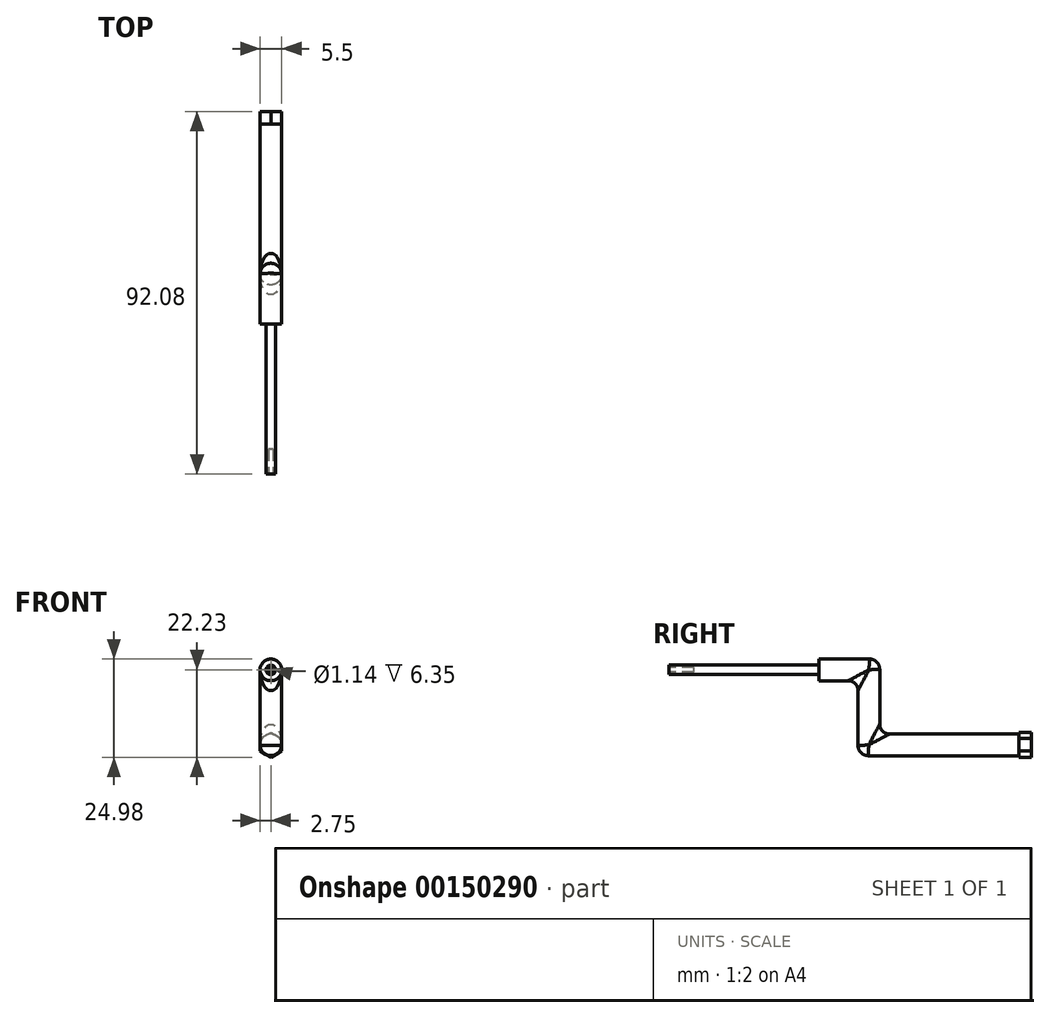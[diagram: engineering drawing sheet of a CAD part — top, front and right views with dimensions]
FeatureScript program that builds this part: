
annotation { "Feature Type Name" : "Feature", "Feature Type Description" : "" }
export const myFeature = defineFeature(function(context is Context, id is Id, definition is map)
    precondition{}
    {
        {
            var Q0;
            Q0=qCreatedBy(makeId("Front.planeOp"),FACE);
            var sketch = newSketch(context, id + "F0", { "sketchPlane" : qUnion([Q0])});
            skCircle(sketch, "E0.cCircle", {"center": v(0, 0) * mm, "radius": 3.18 * mm, "construction": true});
            skLineSegment(sketch, "E0.0", {"start": v(0, 3.18) * mm, "end": v(2.75, 1.59) * mm});
            skLineSegment(sketch, "E0.1", {"start": v(2.75, 1.59) * mm, "end": v(2.75, -1.59) * mm});
            skLineSegment(sketch, "E0.2", {"start": v(2.75, -1.59) * mm, "end": v(0, -3.18) * mm});
            skLineSegment(sketch, "E0.3", {"start": v(0, -3.18) * mm, "end": v(-2.75, -1.59) * mm});
            skLineSegment(sketch, "E0.4", {"start": v(-2.75, -1.59) * mm, "end": v(-2.75, 1.59) * mm});
            skLineSegment(sketch, "E0.5", {"start": v(-2.75, 1.59) * mm, "end": v(0, 3.18) * mm});
            skSolve(sketch);
        }
        {
            var Q0;
            Q0=makeQuery(id+"F0.imprint","IMPRINT",FACE,{"disambiguationData":[TD([[makeQuery(id+"F0.imprint","IMPRINT",EDGE,{"derivedFrom":sQuery(id+"F0.wireOp",EDGE,"E0.0")}),-1.0]])]});
            extrude(context, id + "F1", {"entities" : qUnion([Q0]), "depth" : 3.17 * mm});
        }
        {
            var Q0;
            Q0=makeQuery(id+"F1.opExtrude","CAP_FACE",FACE,{"disambiguationData":[OSD([sQuery(id+"F0.wireOp",EDGE,"E0.0"),sQuery(id+"F0.wireOp",EDGE,"E0.1"),sQuery(id+"F0.wireOp",EDGE,"E0.2"),sQuery(id+"F0.wireOp",EDGE,"E0.3"),sQuery(id+"F0.wireOp",EDGE,"E0.4"),sQuery(id+"F0.wireOp",EDGE,"E0.5")])],"isStart":false});
            var sketch = newSketch(context, id + "F2", { "sketchPlane" : qUnion([Q0])});
            skCircle(sketch, "E1", {"center": v(0, 0) * mm, "radius": 2.75 * mm});
            skSolve(sketch);
        }
        {
            var Q0;
            Q0=qCreatedBy(makeId("Right.planeOp"),FACE);
            var sketch = newSketch(context, id + "F3", { "sketchPlane" : qUnion([Q0])});
            skLineSegment(sketch, "E2.0.0", {"start": v(0, 1.59) * mm, "end": v(0, -1.59) * mm});
            skLineSegment(sketch, "E2.0.1", {"start": v(0, -1.59) * mm, "end": v(-3.18, -1.59) * mm});
            skLineSegment(sketch, "E2.0.2", {"start": v(-3.18, -1.59) * mm, "end": v(-3.18, 1.59) * mm});
            skLineSegment(sketch, "E2.0.3", {"start": v(-3.18, 1.59) * mm, "end": v(0, 1.59) * mm});
            skLineSegment(sketch, "E3", {"start": v(-3.18, 0) * mm, "end": v(-41.27, 0) * mm});
            skPoint(sketch, "E3.endSnap0", {"position": v(-3.18, 0) * mm});
            skLineSegment(sketch, "E4", {"start": v(-41.27, 0) * mm, "end": v(-41.27, 19.05) * mm});
            skLineSegment(sketch, "E5", {"start": v(-41.27, 19.05) * mm, "end": v(-92.08, 19.05) * mm});
            skSolve(sketch);
        }
        {
            var Q0;
            {var subQ0=sQuery(id+"F2.wireOp",EDGE,"E1");var subQ4=makeQuery(id+"F2.imprint","INTERSECT",VERTEX,{"derivedFrom":[makeQuery(id+"F1.opExtrude","CAP_EDGE",EDGE,{"disambiguationData":[OSD([sQuery(id+"F0.wireOp",EDGE,"E0.0")])],"isStart":false}),subQ0]});Q0=makeQuery(id+"F2.imprint","IMPRINT",FACE,{"disambiguationData":[TD([[makeQuery(id+"F2.imprint","IMPRINT",EDGE,{"disambiguationData":[TD([[subQ4,1.0]])],"derivedFrom":subQ0}),1.0]])]});}
            var Q1;
            Q1=sQuery(id+"F3.wireOp",EDGE,"E3");
            var Q2;
            Q2=sQuery(id+"F3.wireOp",EDGE,"E4");
            var Q3;
            Q3=sQuery(id+"F3.wireOp",EDGE,"E5");
            sweep(context, id + "F4", {"operationType" : NewBodyOperationType.ADD, "profiles" : qUnion([Q0]), "path" : qUnion([Q1, Q2, Q3])});
        }
        {
            var Q0;
            Q0=makeQuery(id+"F4.opSweep","MID_CAP_EDGE",EDGE,{"disambiguationData":[OSD([sQuery(id+"F2.wireOp",EDGE,"E1"),sQuery(id+"F3.wireOp",VERTEX,"E5.start")])],"capPos":2.0});
            var Q1;
            Q1=makeQuery(id+"F4.opSweep","MID_CAP_EDGE",EDGE,{"disambiguationData":[OSD([sQuery(id+"F2.wireOp",EDGE,"E1"),sQuery(id+"F3.wireOp",VERTEX,"E4.start")])],"capPos":1.0});
            fillet(context, id + "F5", {"entities" : qUnion([Q0, Q1]), "radius" : 2.54 * mm, "tangentPropagation" : true, "allowEdgeOverflow" : false});
        }
        {
            var Q0;
            Q0=qCreatedBy(makeId("Right.planeOp"),FACE);
            var sketch = newSketch(context, id + "F6", { "sketchPlane" : qUnion([Q0])});
            skLineSegment(sketch, "E6.bottom", {"start": v(-53.98, 17.84) * mm, "end": v(-92.08, 17.84) * mm});
            skLineSegment(sketch, "E6.top", {"start": v(-53.98, 14.72) * mm, "end": v(-92.08, 14.72) * mm});
            skLineSegment(sketch, "E6.left", {"start": v(-53.98, 17.84) * mm, "end": v(-53.98, 14.72) * mm});
            skLineSegment(sketch, "E6.right", {"start": v(-92.08, 17.84) * mm, "end": v(-92.08, 14.72) * mm});
            skLineSegment(sketch, "E7", {"start": v(-92.07, 21.8) * mm, "end": v(-41.07, 21.8) * mm});
            skLineSegment(sketch, "E8", {"start": v(-46.56, 16.3) * mm, "end": v(-92.07, 16.3) * mm});
            skLineSegment(sketch, "E9.0", {"start": v(-92.08, 16.3) * mm, "end": v(-92.08, 21.8) * mm});
            skLineSegment(sketch, "E10", {"start": v(-92.08, 19.05) * mm, "end": v(-79.38, 19.05) * mm});
            skPoint(sketch, "E10.endSnap0", {"position": v(-92.08, 19.05) * mm});
            skSolve(sketch);
        }
        {
            var Q0;
            Q0 = qSketchRegion(id + "F6", true);
            var Q1;
            Q1=sQuery(id+"F6.wireOp",EDGE,"E10");
            revolve(context, id + "F7", {"operationType" : NewBodyOperationType.REMOVE, "entities" : qUnion([Q0]), "axis" : qUnion([Q1]), "revolveType" : RevolveType.FULL, "oppositeDirection" : true});
        }
        {
            var Q0;
            Q0=makeQuery(id+"F4.opSweep","CAP_FACE",FACE,{"disambiguationData":[OSD([sQuery(id+"F2.wireOp",EDGE,"E1"),sQuery(id+"F3.wireOp",VERTEX,"E5.end")])],"isStart":false});
            var sketch = newSketch(context, id + "F8", { "sketchPlane" : qUnion([Q0])});
            skCircle(sketch, "E11", {"center": v(0, 19.05) * mm, "radius": 1.2 * mm});
            skCircle(sketch, "E12.0.0", {"center": v(0, 19.05) * mm, "radius": 2.75 * mm});
            skCircle(sketch, "E13", {"center": v(0, 19.05) * mm, "radius": 0.57 * mm});
            skSolve(sketch);
        }
        {
            var Q0;
            Q0=makeQuery(id+"F8.imprint","IMPRINT",FACE,{"disambiguationData":[TD([[makeQuery(id+"F8.imprint","IMPRINT",EDGE,{"derivedFrom":sQuery(id+"F8.wireOp",EDGE,"E13")}),1.0]])]});
            extrude(context, id + "F9", {"entities" : qUnion([Q0]), "operationType" : NewBodyOperationType.REMOVE, "oppositeDirection" : true, "depth" : 6.35 * mm});
        }
    });
